# Revit family: НЕВАТОМ_Вентилятор VKK 100-315, версия 1
name_source: partatom
category: Оборудование
revit_build: Autodesk Revit 2017 (Build: 20170118_1100(x64)
units: mm (PartAtom-declared; Revit-internal decimal feet)

## family parameters
Всегда вертикально = Да
На основе рабочей плоскости = Нет
Общий = Нет
При загрузке вырезать с полостями = Нет
Размер круглого соединителя = Использовать диаметр
Тип детали = Вставляется
Точка расчета площади = Нет

## types (6) — shared parameters
ADSK_Единица измерения = шт.
ADSK_Завод-изготовитель = НЕВАТОМ
ADSK_Количество = 1
ADSK_Материал наименование = Оцинкованная сталь
ADSK_Наименование = Вентилятор канальный круглый
ADSK_Напряжение = 230 В
ADSK_Полная мощность = 0 кВт
B = 170 мм
H = 53 мм
Nevatom_URL = https://t.me
Ключевая пометка = Вентиляция
Крышка = СВМПЭ, белый
Материал = Сталь серая

## per-type parameters (varying)
| type | 2h | A | ADSK_Масса | ADSK_Масса_Текст | ADSK_Размер_Высота | ADSK_Размер_Длина | ADSK_Размер_Ширина | ADSK_Ток | ADSK_Частота вращения вентилятора | D | L | d | d/2 | h | Макс. расход воздуха | Полное давление |
| VKK - 100m | 46 мм | 275 мм | 3.2 | 3,2 | 295 мм | 242 мм | 195 мм | 0 А | 2500 | 242 мм | 195 мм | 97 мм | 49 мм | 23 мм | 230.0 м³/ч | 260.0 Па |
| VKK - 315m | 52 мм | 435 мм | 6.1 | 6,1 | 455 мм | 402 мм | 235 мм | 1 А | 2500 | 402 мм | 235 мм | 315 мм | 158 мм | 26 мм | 1750.0 м³/ч | 690.0 Па |
| VKK - 125m | 52 мм | 275 мм | 3.4 | 3,4 | 295 мм | 242 мм | 190 мм | 0 А | 2400 | 242 мм | 190 мм | 125 мм | 63 мм | 26 мм | 360.0 м³/ч | 270.0 Па |
| VKK - 160m | 52 мм | 365 мм | 4.7 | 4,7 | 385 мм | 332 мм | 232 мм | 1 А | 2550 | 332 мм | 232 мм | 160 мм | 80 мм | 26 мм | 700.0 м³/ч | 380.0 Па |
| VKK - 200m | 46 мм | 365 мм | 5.1 | 5,1 | 385 мм | 332 мм | 228 мм | 1 А | 2600 | 332 мм | 228 мм | 198 мм | 99 мм | 23 мм | 850.0 м³/ч | 460.0 Па |
| VKK - 250m | 52 мм | 365 мм | 4.8 | 4,8 | 385 мм | 332 мм | 210 мм | 1 А | 2500 | 332 мм | 210 мм | 248 мм | 124 мм | 26 мм | 1085.0 м³/ч | 525.0 Па |

note: column(s) folded — value = type name in every type: ADSK_Марка
